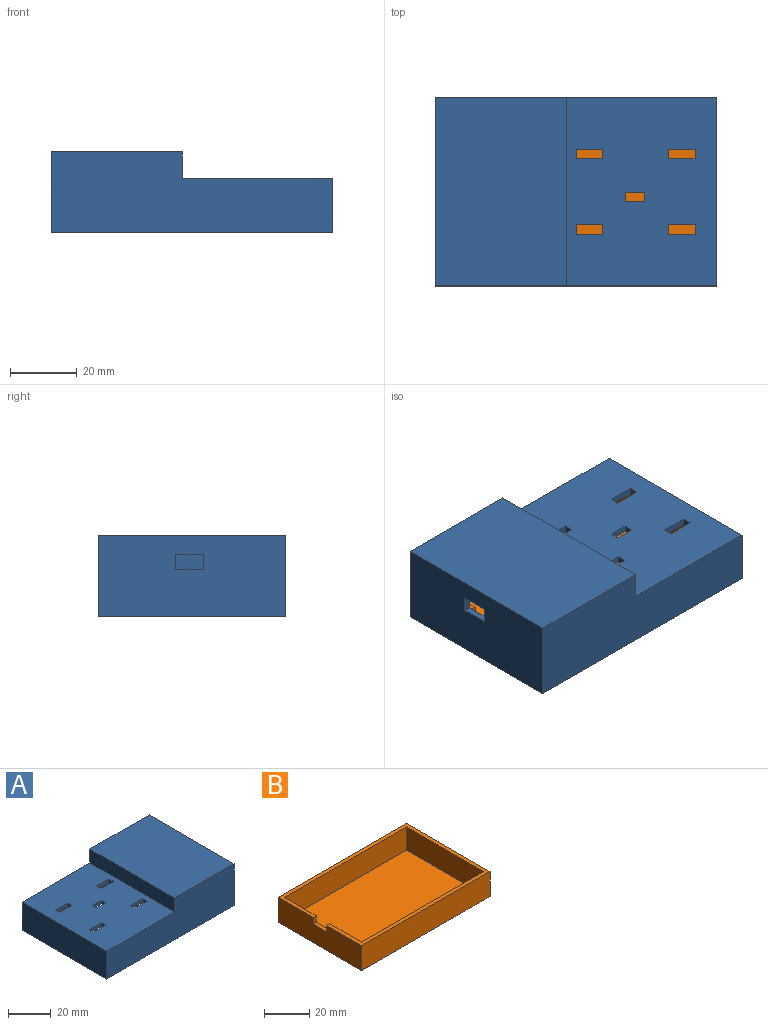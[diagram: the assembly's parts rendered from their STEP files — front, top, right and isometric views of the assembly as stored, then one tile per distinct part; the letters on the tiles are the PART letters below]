
ASSEMBLY  parts=2 mates=1
PART A: 39 faces, bbox 84.3x56.3x24 mm
  f0: plane 52.25x44.75mm, normal (0,0,-1), area 2234.4mm2, adj f8,f10,f11,f12,f15,f16,f17,f18
  f1: plane 56.25x45mm, normal (0,0,1), area 2427.4mm2, adj f3,f5,f6,f14,f15,f16,f17,f18
  f2: plane 56.25x39.25mm, normal (0,0,1), area 2207.8mm2, adj f3,f6,f7,f14
  f3: plane 84.25x24mm, normal (0,1,0), area 1662mm2, adj f1,f2,f4,f5,f7,f14
  f4: plane 84.25x56.25mm, normal (0,0,-1), area 546mm2, adj f3,f5,f6,f7,f8,f9,f10,f11
  f5: plane 56.25x16mm, normal (-1,0,0), area 900mm2, adj f1,f3,f4,f6
  f6: plane 84.25x24mm, normal (0,-1,0), area 1662mm2, adj f1,f2,f4,f5,f7,f14
  f7: plane 56.25x24mm, normal (1,0,0), area 1312.9mm2, adj f2,f3,f4,f6,f35,f36,f37,f38
  f8: plane 80.25x22mm, normal (0,-1,0), area 1407.5mm2, adj f0,f4,f9,f11,f12,f13
  f9: plane 52.25x22mm, normal (-1,0,0), area 1112.4mm2, adj f4,f8,f10,f13,f35,f36,f37,f38
  f10: plane 80.25x22mm, normal (0,1,0), area 1407.5mm2, adj f0,f4,f9,f11,f12,f13
  f11: plane 52.25x14mm, normal (1,0,0), area 731.5mm2, adj f0,f4,f8,f10
  f12: plane 52.25x8mm, normal (1,0,0), area 418mm2, adj f0,f8,f10,f13
  f13: plane 52.25x35.5mm, normal (0,0,-1), area 1854.9mm2, adj f8,f9,f10,f12
  f14: plane 56.25x8mm, normal (-1,0,0), area 450mm2, adj f1,f2,f3,f6
  f15: plane 2.75x2mm, normal (1,0,0), area 5.5mm2, adj f0,f1,f16,f18
  f16: plane 8x2mm, normal (0,-1,0), area 16mm2, adj f0,f1,f15,f17
  f17: plane 2.75x2mm, normal (-1,0,0), area 5.5mm2, adj f0,f1,f16,f18
  f18: plane 8x2mm, normal (0,1,0), area 16mm2, adj f0,f1,f15,f17
  f19: plane 2.75x2mm, normal (1,0,0), area 5.5mm2, adj f0,f1,f20,f22
  f20: plane 5.75x2mm, normal (0,-1,0), area 11.5mm2, adj f0,f1,f19,f21
  f21: plane 2.75x2mm, normal (-1,0,0), area 5.5mm2, adj f0,f1,f20,f22
  f22: plane 5.75x2mm, normal (0,1,0), area 11.5mm2, adj f0,f1,f19,f21
  f23: plane 2.75x2mm, normal (1,0,0), area 5.5mm2, adj f0,f1,f24,f26
  f24: plane 8x2mm, normal (0,-1,0), area 16mm2, adj f0,f1,f23,f25
  f25: plane 2.75x2mm, normal (-1,0,0), area 5.5mm2, adj f0,f1,f24,f26
  f26: plane 8x2mm, normal (0,1,0), area 16mm2, adj f0,f1,f23,f25
  f27: plane 8x2mm, normal (0,-1,0), area 16mm2, adj f0,f1,f28,f30
  f28: plane 2.75x2mm, normal (-1,0,0), area 5.5mm2, adj f0,f1,f27,f29
  f29: plane 8x2mm, normal (0,1,0), area 16mm2, adj f0,f1,f28,f30
  f30: plane 2.75x2mm, normal (1,0,0), area 5.5mm2, adj f0,f1,f27,f29
  f31: plane 8x2mm, normal (0,1,0), area 16mm2, adj f0,f1,f32,f34
  f32: plane 2.75x2mm, normal (1,0,0), area 5.5mm2, adj f0,f1,f31,f33
  f33: plane 8x2mm, normal (0,-1,0), area 16mm2, adj f0,f1,f32,f34
  f34: plane 2.75x2mm, normal (-1,0,0), area 5.5mm2, adj f0,f1,f31,f33
  f35: plane 4.5x2mm, normal (0,1,0), area 9mm2, adj f7,f9,f36,f38
  f36: plane 8.25x2mm, normal (0,0,1), area 16.5mm2, adj f7,f9,f35,f37
  f37: plane 4.5x2mm, normal (0,-1,0), area 9mm2, adj f7,f9,f36,f38
  f38: plane 8.25x2mm, normal (0,0,-1), area 16.5mm2, adj f7,f9,f35,f37
PART B: 14 faces, bbox 80x52.3x13.5 mm
  f0: plane 80x52.25mm, normal (0,0,1), area 486.4mm2, adj f1,f2,f3,f4,f5,f7,f8,f9
  f1: plane 52.25x13.5mm, normal (-1,0,0), area 675.6mm2, adj f0,f3,f4,f6,f11,f12,f13
  f2: plane 48.26x12.5mm, normal (1,0,0), area 573.5mm2, adj f0,f7,f9,f10,f11,f12,f13
  f3: plane 80x13.5mm, normal (0,1,0), area 1080mm2, adj f0,f1,f5,f6
  f4: plane 80x13.5mm, normal (0,-1,0), area 1080mm2, adj f0,f1,f5,f6
  f5: plane 52.25x13.5mm, normal (1,0,0), area 705.4mm2, adj f0,f3,f4,f6
  f6: plane 80x52.25mm, normal (0,0,-1), area 4180mm2, adj f1,f3,f4,f5
  f7: plane 76.2x12.5mm, normal (0,1,0), area 952.5mm2, adj f0,f2,f8,f10
  f8: plane 48.26x12.5mm, normal (-1,0,0), area 603.2mm2, adj f0,f7,f9,f10
  f9: plane 76.2x12.5mm, normal (0,-1,0), area 952.5mm2, adj f0,f2,f8,f10
  f10: plane 76.2x48.26mm, normal (0,0,1), area 3677.4mm2, adj f2,f7,f8,f9
  f11: plane 8.5x1.9mm, normal (0,0,1), area 16.1mm2, adj f1,f2,f12,f13
  f12: plane 3.5x1.9mm, normal (0,-1,0), area 6.6mm2, adj f0,f1,f2,f11
  f13: plane 3.5x1.9mm, normal (0,1,0), area 6.6mm2, adj f0,f1,f2,f11
PLACE A rot(axis=(0,0,1),180deg) t=(82.5,54.25,-0.19)mm
PLACE B at identity fixed
MATE slider A.f13 <-> B.f10  axis (0,0,-1) through (18,26.13,21.81)mm
